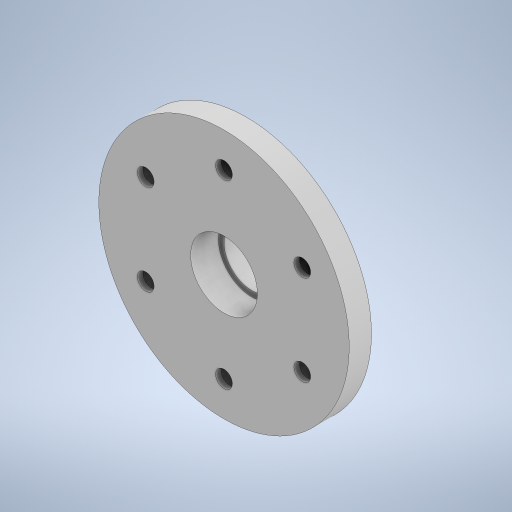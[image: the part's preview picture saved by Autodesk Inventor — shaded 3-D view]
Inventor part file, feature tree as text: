
AUTODESK INVENTOR PART (.ipt)
format: ipt  version: 2023 (Build 270158000, 158)  size: 302,080 bytes
history: native  units: in
note: dims shown in document units (in); Inventor stores cm internally (conversion verified against a paired STEP export)
features: sketch x4, extrude x4, plane x2, other x2, hole x1
ambient origin geometry x8: Origin, YZ Plane, XZ Plane, XY Plane, X Axis, Y Axis, Z Axis, Center Point
bodies: Solid1 (feature_tree)
feature tree (13):
  plane  "Work Plane1"
  sketch  "Sketch1"  dims[d0=1.375in d1=2.5591in]
  extrude  "Extrusion1"  Depth=2.5591in
  plane  "Work Plane2"
  extrude  "Extrusion2"  Depth=0.3543in
  extrude  "Extrusion3"  Depth=0.315in TaperAngle=0.0deg
  hole  "Hole1"  [1 undecoded]
  extrude  "Extrusion4"  Depth=0.2362in
  sketch  "Sketch3"  dims[d2=3.5433in d3=0.3543in]
  sketch  "Sketch4"  dims[d4=2.3622in d6=360.0deg d8=0.315in d9=0.0in]
  sketch  "Sketch5"  dims[d10=0.6225in d11=0.0in d12=0.2362in d13=0.2362in d14=0.2362in d15=0.2362in d16=0.2362in d17=0.2362in d18=0.0787in d19=0.0in d20=0.7874in d21=0.2362in d22=0.9449in d23=0.3937in d24=90.0deg d25=0.315in d26=0.8108in d27=0.0984in d28=0.0394in d29=0.0in]
  other  "Assembly1"
  other  "177x35x10 bearing:1"
note: 1 required parameter value undecoded (feature->parameter linkage not recoverable at this tier; creation-order binding heuristic only, values carry confidence <= 0.55)
